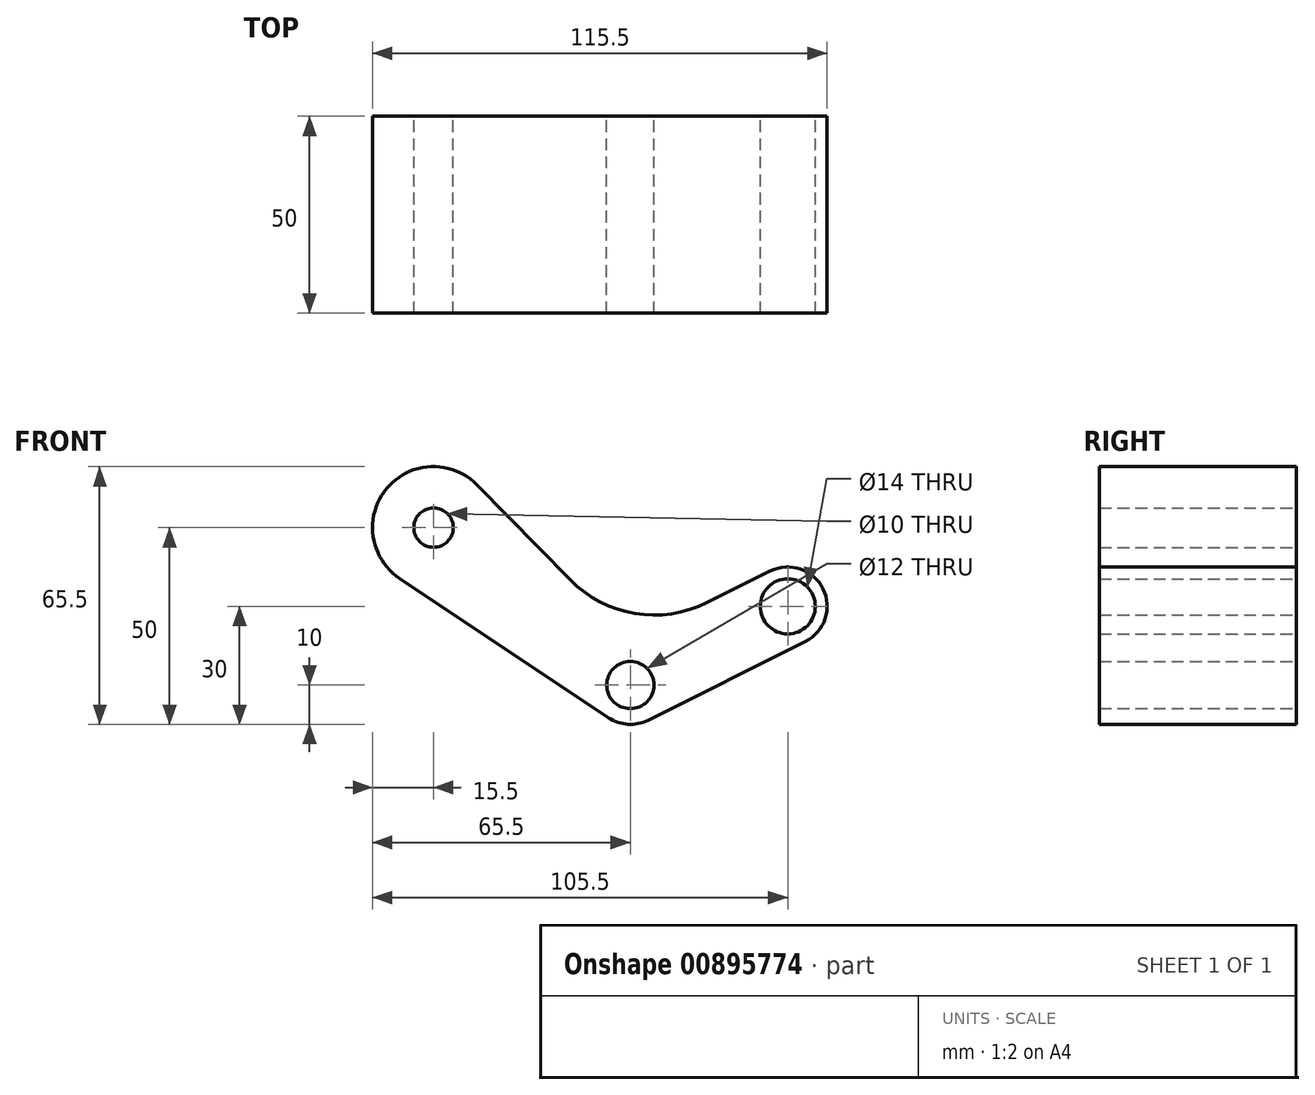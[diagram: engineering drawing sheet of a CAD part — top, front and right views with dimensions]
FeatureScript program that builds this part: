
annotation { "Feature Type Name" : "Feature", "Feature Type Description" : "" }
export const myFeature = defineFeature(function(context is Context, id is Id, definition is map)
    precondition{}
    {
        {
            var Q0;
            Q0=qCreatedBy(makeId("Front.planeOp"),FACE);
            var sketch = newSketch(context, id + "F0", { "sketchPlane" : qUnion([Q0])});
            skCircle(sketch, "E0", {"center": v(0, 0) * mm, "radius": 6 * mm});
            skCircle(sketch, "E1", {"center": v(0, 0) * mm, "radius": 10 * mm});
            skCircle(sketch, "E2", {"center": v(-50, 40) * mm, "radius": 15.5 * mm});
            skCircle(sketch, "E3", {"center": v(-50, 40) * mm, "radius": 5 * mm});
            skCircle(sketch, "E4", {"center": v(40, 20) * mm, "radius": 10 * mm});
            skCircle(sketch, "E5", {"center": v(40, 20) * mm, "radius": 7 * mm});
            skLineSegment(sketch, "E6", {"start": v(-38.94, 50.86) * mm, "end": v(-15.3, 26.77) * mm});
            skLineSegment(sketch, "E7", {"start": v(19.53, 20.95) * mm, "end": v(35.53, 28.94) * mm});
            skLineSegment(sketch, "E8", {"start": v(4.47, -8.94) * mm, "end": v(44.47, 11.06) * mm});
            skLineSegment(sketch, "E9", {"start": v(-58.6, 27.1) * mm, "end": v(-5.55, -8.32) * mm});
            skPoint(sketch, "E10.visualSharp", {"position": v(0, 11.18) * mm});
            skArc(sketch, "E10.filletArc", {"start": v(-15.3, 26.77) * mm, "mid": v(1.17, 18.19) * mm, "end": v(19.53, 20.95) * mm});
            skSolve(sketch);
        }
        {
            var Q0;
            Q0=makeQuery(id+"F0.imprint","IMPRINT",FACE,{"disambiguationData":[TD([[makeQuery(id+"F0.imprint","IMPRINT",EDGE,{"derivedFrom":sQuery(id+"F0.wireOp",EDGE,"E3")}),-1.0]])]});
            var Q1;
            {var subQ3=sQuery(id+"F0.wireOp",EDGE,"E6");Q1=makeQuery(id+"F0.imprint","IMPRINT",FACE,{"disambiguationData":[TD([[makeQuery(id+"F0.imprint","IMPRINT",EDGE,{"derivedFrom":subQ3}),-1.0]])]});}
            var Q2;
            Q2=makeQuery(id+"F0.imprint","IMPRINT",FACE,{"disambiguationData":[TD([[makeQuery(id+"F0.imprint","IMPRINT",EDGE,{"derivedFrom":sQuery(id+"F0.wireOp",EDGE,"E0")}),-1.0]])]});
            var Q3;
            Q3=makeQuery(id+"F0.imprint","IMPRINT",FACE,{"disambiguationData":[TD([[makeQuery(id+"F0.imprint","IMPRINT",EDGE,{"derivedFrom":sQuery(id+"F0.wireOp",EDGE,"E5")}),-1.0]])]});
            extrude(context, id + "F1", {"entities" : qUnion([Q0, Q1, Q2, Q3]), "endBound" : BoundingType.SYMMETRIC, "depth" : 50 * mm, "offsetDistance" : 25 * mm});
        }
    });
